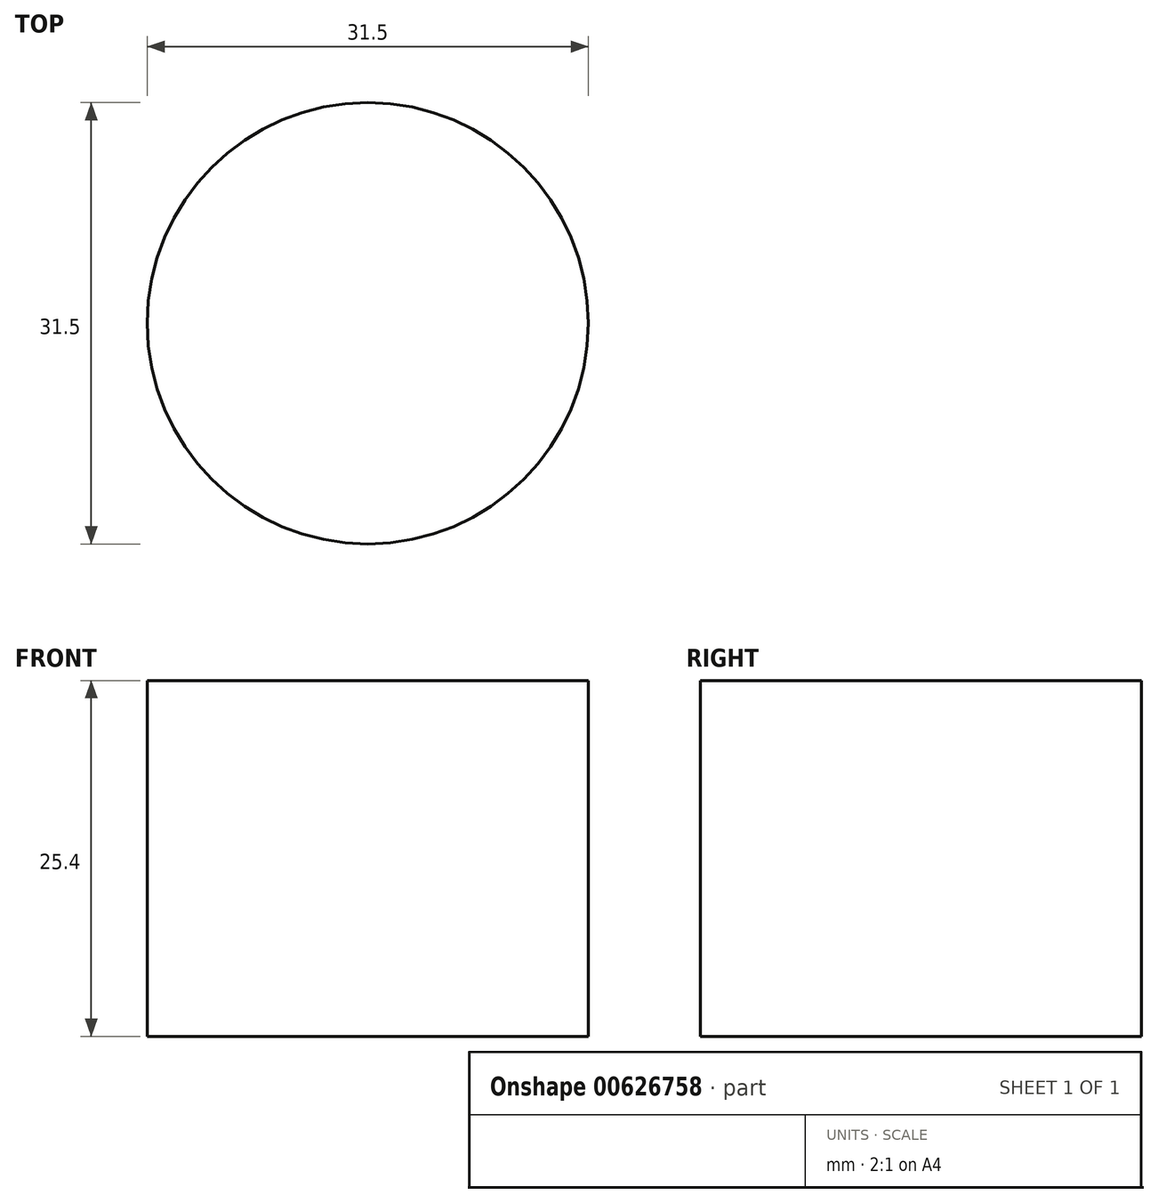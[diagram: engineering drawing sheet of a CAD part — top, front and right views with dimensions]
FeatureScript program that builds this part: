
annotation { "Feature Type Name" : "Feature", "Feature Type Description" : "" }
export const myFeature = defineFeature(function(context is Context, id is Id, definition is map)
    precondition{}
    {
        {
            var Q0;
            Q0=qCreatedBy(makeId("Top.planeOp"),FACE);
            var sketch = newSketch(context, id + "F0", { "sketchPlane" : qUnion([Q0])});
            skCircle(sketch, "E0", {"center": v(0, 0) * mm, "radius": 15.75 * mm});
            skCircle(sketch, "E1", {"center": v(-10.92, -11.35) * mm, "radius": 127.68 * mm});
            skCircle(sketch, "E2", {"center": v(113.1, 18.99) * mm, "radius": 14.72 * mm});
            skCircle(sketch, "E3", {"center": v(125.83, 26.38) * mm, "radius": 10.22 * mm});
            skSolve(sketch);
        }
        {
            var Q0;
            Q0=sQuery(id+"F0.wireOp",EDGE,"E0");
            extrude(context, id + "F1", {"bodyType" : ToolBodyType.SURFACE, "surfaceEntities" : qUnion([Q0]), "depth" : 25.4 * mm, "offsetDistance" : 25.4 * mm});
        }
    });
